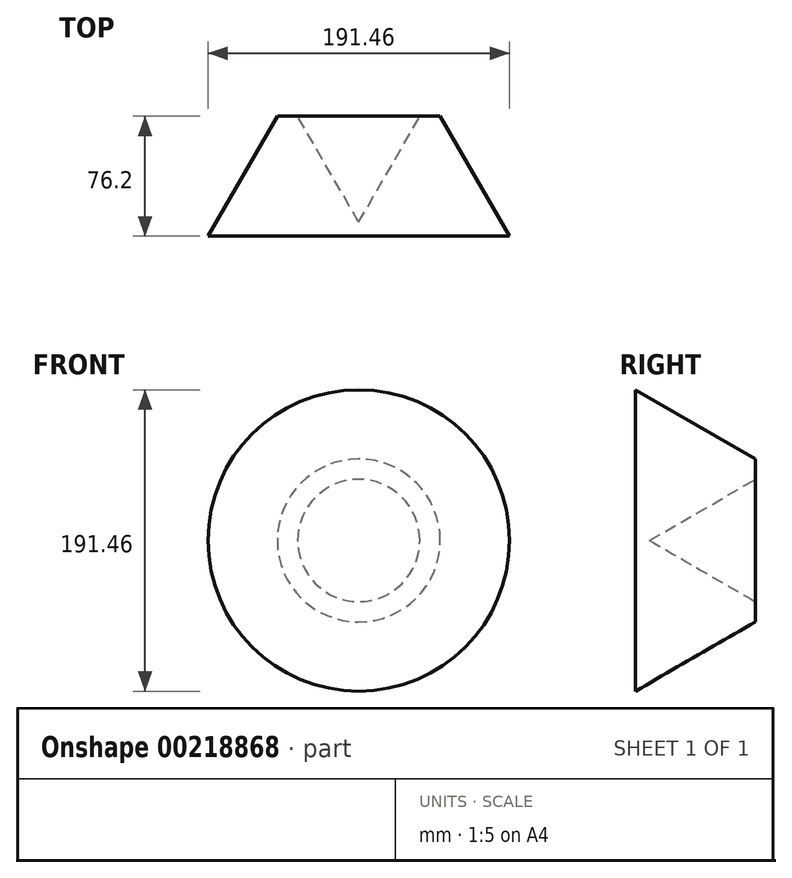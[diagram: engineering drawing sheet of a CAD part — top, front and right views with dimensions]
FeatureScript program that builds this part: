
annotation { "Feature Type Name" : "Feature", "Feature Type Description" : "" }
export const myFeature = defineFeature(function(context is Context, id is Id, definition is map)
    precondition{}
    {
        {
            var Q0;
            Q0=qCreatedBy(makeId("Front.planeOp"),FACE);
            var sketch = newSketch(context, id + "F0", { "sketchPlane" : qUnion([Q0])});
            skCircle(sketch, "E0", {"center": v(0, 0) * mm, "radius": 51.74 * mm});
            skCircle(sketch, "E1", {"center": v(0, 0) * mm, "radius": 38.82 * mm});
            skSolve(sketch);
        }
        {
            var Q0;
            Q0=makeQuery(id+"F0.imprint","IMPRINT",FACE,{"disambiguationData":[TD([[makeQuery(id+"F0.imprint","IMPRINT",EDGE,{"derivedFrom":sQuery(id+"F0.wireOp",EDGE,"E0")}),1.0]])]});
            extrude(context, id + "F1", {"entities" : qUnion([Q0]), "depth" : 76.2 * mm, "hasDraft" : true, "draftAngle" : 30 * degree});
        }
    });
